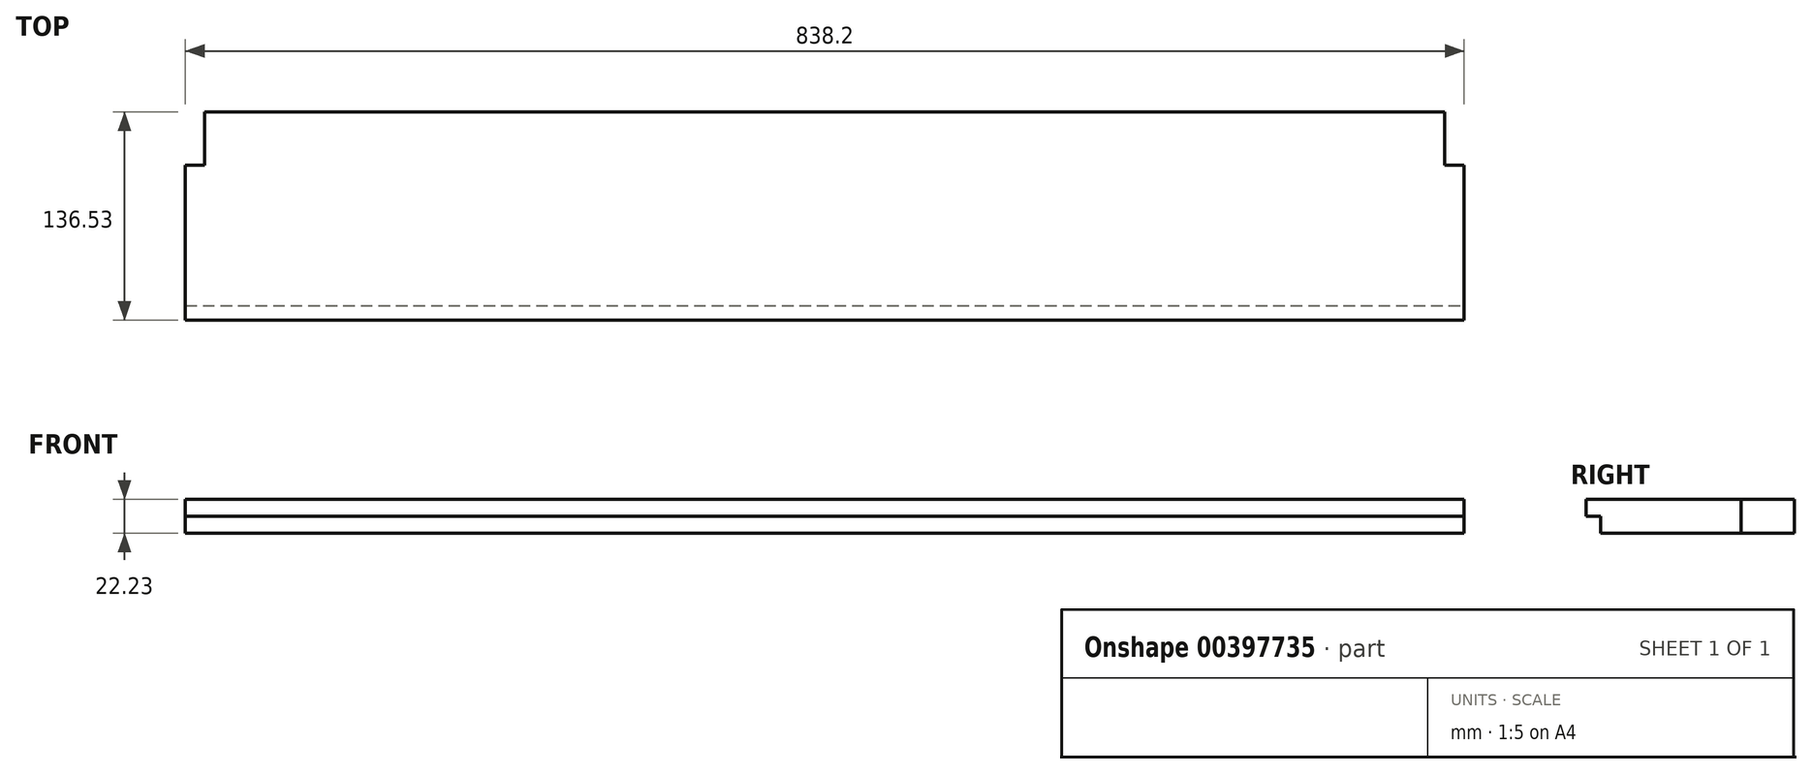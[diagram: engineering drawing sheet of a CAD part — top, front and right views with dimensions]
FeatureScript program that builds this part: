
annotation { "Feature Type Name" : "Feature", "Feature Type Description" : "" }
export const myFeature = defineFeature(function(context is Context, id is Id, definition is map)
    precondition{}
    {
        {
            var Q0;
            Q0=qCreatedBy(makeId("Top.planeOp"),FACE);
            var sketch = newSketch(context, id + "F0", { "sketchPlane" : qUnion([Q0])});
            skLineSegment(sketch, "E0.bottom", {"start": v(0, 0) * mm, "end": v(838.2, 0) * mm});
            skLineSegment(sketch, "E0.left", {"start": v(0, 0) * mm, "end": v(0, 101.6) * mm});
            skLineSegment(sketch, "E1.top", {"start": v(0, 101.6) * mm, "end": v(12.7, 101.6) * mm});
            skLineSegment(sketch, "E1.right", {"start": v(12.7, 136.53) * mm, "end": v(12.7, 101.6) * mm});
            skLineSegment(sketch, "E2.top", {"start": v(825.5, 101.6) * mm, "end": v(838.2, 101.6) * mm});
            skLineSegment(sketch, "E2.left", {"start": v(825.5, 136.53) * mm, "end": v(825.5, 101.6) * mm});
            skLineSegment(sketch, "E3", {"start": v(12.7, 136.53) * mm, "end": v(825.5, 136.53) * mm});
            skLineSegment(sketch, "E4", {"start": v(838.2, 101.6) * mm, "end": v(838.2, 0) * mm});
            skSolve(sketch);
        }
        {
            var Q0;
            Q0=makeQuery(id+"F0.imprint","IMPRINT",FACE,{"disambiguationData":[TD([[makeQuery(id+"F0.imprint","IMPRINT",EDGE,{"derivedFrom":sQuery(id+"F0.wireOp",EDGE,"E0.bottom")}),1.0]])]});
            extrude(context, id + "F1", {"entities" : qUnion([Q0]), "depth" : 22.22 * mm});
        }
        {
            var Q0;
            Q0=makeQuery(id+"F1.opExtrude","CAP_FACE",FACE,{"disambiguationData":[OSD([sQuery(id+"F0.wireOp",EDGE,"E0.bottom"),sQuery(id+"F0.wireOp",EDGE,"E0.left"),sQuery(id+"F0.wireOp",EDGE,"E1.top"),sQuery(id+"F0.wireOp",EDGE,"E1.right"),sQuery(id+"F0.wireOp",EDGE,"E2.top"),sQuery(id+"F0.wireOp",EDGE,"E2.left"),sQuery(id+"F0.wireOp",EDGE,"E3"),sQuery(id+"F0.wireOp",EDGE,"E4")])],"isStart":true});
            var sketch = newSketch(context, id + "F2", { "sketchPlane" : qUnion([Q0])});
            skLineSegment(sketch, "E5.bottom", {"start": v(0, 0) * mm, "end": v(838.2, 0) * mm});
            skLineSegment(sketch, "E5.top", {"start": v(0, -9.52) * mm, "end": v(838.2, -9.52) * mm});
            skLineSegment(sketch, "E5.left", {"start": v(0, 0) * mm, "end": v(0, -9.52) * mm});
            skLineSegment(sketch, "E5.right", {"start": v(838.2, 0) * mm, "end": v(838.2, -9.52) * mm});
            skSolve(sketch);
        }
        {
            var Q0;
            Q0=makeQuery(id+"F2.imprint","IMPRINT",FACE,{"disambiguationData":[TD([[makeQuery(id+"F2.imprint","IMPRINT",EDGE,{"derivedFrom":sQuery(id+"F2.wireOp",EDGE,"E5.bottom")}),-1.0]])]});
            extrude(context, id + "F3", {"entities" : qUnion([Q0]), "operationType" : NewBodyOperationType.REMOVE, "oppositeDirection" : true, "depth" : 11.1 * mm});
        }
    });
